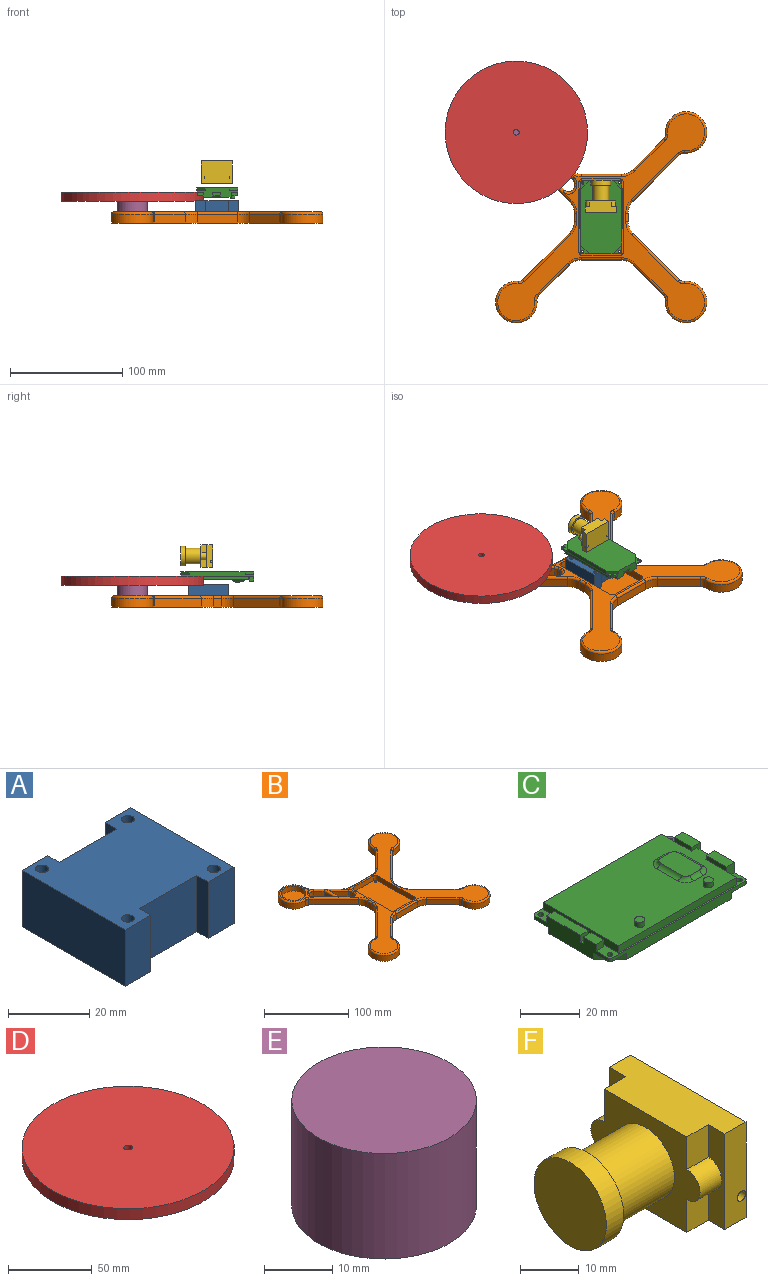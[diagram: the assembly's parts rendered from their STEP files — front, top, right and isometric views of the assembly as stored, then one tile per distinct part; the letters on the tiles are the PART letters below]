
ASSEMBLY  parts=6 mates=3
PART A: 18 faces, bbox 38x36x17 mm
  f0: plane 36x17.02mm, normal (1,0,0), area 612.6mm2, adj f1,f15,f16,f17
  f1: plane 17.02x9mm, normal (0,1,0), area 153.2mm2, adj f0,f2,f16,f17
  f2: plane 17.02x4mm, normal (-1,0,0), area 68.1mm2, adj f1,f3,f16,f17
  f3: plane 20x17.02mm, normal (0,1,0), area 340.4mm2, adj f2,f4,f16,f17
  f4: plane 17.02x4mm, normal (1,0,0), area 68.1mm2, adj f3,f5,f16,f17
  f5: plane 17.02x9mm, normal (0,1,0), area 153.2mm2, adj f4,f6,f16,f17
  f6: plane 36x17.02mm, normal (-1,0,0), area 612.6mm2, adj f5,f7,f16,f17
  f7: plane 17.02x9mm, normal (0,-1,0), area 153.2mm2, adj f6,f8,f16,f17
  f8: plane 17.02x4mm, normal (1,0,0), area 68.1mm2, adj f7,f9,f16,f17
  f9: plane 20x17.02mm, normal (0,-1,0), area 340.4mm2, adj f8,f10,f16,f17
  f10: plane 17.02x4mm, normal (-1,0,0), area 68.1mm2, adj f9,f15,f16,f17
  f11: cylinder r=1.6mm len=17.02mm, axis (0,0,-1), area 171.1mm2, adj f16,f17
  f12: cylinder r=1.6mm len=17.02mm, axis (0,0,-1), area 171.1mm2, adj f16,f17
  f13: cylinder r=1.6mm len=17.02mm, axis (0,0,-1), area 171.1mm2, adj f16,f17
  f14: cylinder r=1.6mm len=17.02mm, axis (0,0,-1), area 171.1mm2, adj f16,f17
  f15: plane 17.02x9mm, normal (0,-1,0), area 153.2mm2, adj f0,f10,f16,f17
  f16: plane 38x36mm, normal (0,0,1), area 1175.8mm2, adj f0,f1,f2,f3,f4,f5,f6,f7
  f17: plane 38x36mm, normal (0,0,-1), area 1175.8mm2, adj f0,f1,f2,f3,f4,f5,f6,f7
PART B: 109 faces, bbox 191.4x191.4x10 mm
  f0: plane 184.37x184.37mm, normal (0,0,1), area 6055.4mm2, adj f27,f28,f29,f30,f55,f56,f57,f60
  f1: plane 8.81x8.81mm, normal (0.71,0.71,0), area 99.6mm2, adj f4,f51,f68,f99
  f2: plane 8.87x8.87mm, normal (-0.71,-0.71,0), area 100.4mm2, adj f4,f53,f55,f93
  f3: plane 38.8x38.8mm, normal (0,0,1), area 230.2mm2, adj f25,f54,f55,f58,f59,f62,f63,f67
  f4: plane 188.37x188.37mm, normal (0,0,-1), area 11909.2mm2, adj f1,f2,f5,f6,f7,f8,f9,f10
  f5: plane 41.52x41.52mm, normal (-0.71,0.71,0), area 469.8mm2, adj f4,f40,f42,f77
  f6: plane 27.32x27.32mm, normal (0.71,-0.71,0), area 309.1mm2, adj f4,f34,f43,f85
  f7: plane 27.32x27.32mm, normal (-0.71,-0.71,0), area 309.1mm2, adj f4,f35,f44,f92
  f8: plane 41.52x41.52mm, normal (-0.71,-0.71,0), area 469.8mm2, adj f4,f41,f49,f68
  f9: cylinder r=18.53mm len=37.05mm, axis (0,0,-1), area 726.3mm2, adj f4,f42,f43,f81
  f10: cylinder r=18.53mm len=37.05mm, axis (0,0,-1), area 726.3mm2, adj f4,f44,f45,f88
  f11: plane 41.52x41.52mm, normal (0.71,0.71,0), area 469.8mm2, adj f4,f36,f45,f84
  f12: plane 41.52x41.52mm, normal (0.71,-0.71,0), area 469.8mm2, adj f4,f37,f46,f76
  f13: cylinder r=18.53mm len=37.05mm, axis (0,0,-1), area 726.3mm2, adj f4,f46,f47,f72
  f14: plane 27.32x27.32mm, normal (-0.71,0.71,0), area 309.1mm2, adj f4,f38,f47,f69
  f15: plane 27.32x27.32mm, normal (0.71,0.71,0), area 309.1mm2, adj f4,f39,f48,f55
  f16: cylinder r=18.53mm len=37.05mm, axis (0,0,-1), area 726.3mm2, adj f4,f48,f49,f62
  f17: plane 8x7.29mm, normal (-1,0,0), area 58.3mm2, adj f4,f40,f41,f73
  f18: plane 35.69x8mm, normal (0,1,0), area 285.5mm2, adj f4,f38,f39,f61
  f19: plane 8x7.29mm, normal (1,0,0), area 58.3mm2, adj f4,f36,f37,f80
  f20: plane 35.69x8mm, normal (0,-1,0), area 285.5mm2, adj f4,f34,f35,f89
  f21: cylinder r=18.53mm len=8mm, axis (0,0,1), area 12.6mm2, adj f4,f50,f53,f59
  f22: plane 15.94x15.94mm, normal (0.71,0.71,0), area 180.4mm2, adj f4,f50,f68,f97
  f23: plane 8x2.83mm, normal (-1,0,0), area 22.6mm2, adj f4,f51,f52,f60
  f24: plane 14.46x14.46mm, normal (-0.71,-0.71,0), area 163.6mm2, adj f4,f52,f55,f95
  f25: cylinder r=14.53mm len=29.05mm, axis (0,0,1), area 638.9mm2, adj f3,f26
  f26: plane 29.05x29.05mm, normal (0,0,1), area 662.8mm2, adj f25
  f27: plane 61.1x7mm, normal (-1,0,0), area 427.7mm2, adj f0,f31,f105,f108
  f28: plane 32.7x7mm, normal (0,-1,0), area 228.9mm2, adj f0,f31,f105,f106
  f29: plane 61.1x7mm, normal (1,0,0), area 427.7mm2, adj f0,f31,f106,f107
  f30: plane 32.7x7mm, normal (0,1,0), area 228.9mm2, adj f0,f31,f107,f108
  f31: plane 68.4x40mm, normal (0,0,1), area 2712mm2, adj f27,f28,f29,f30,f101,f102,f103,f104
  f32: plane 14.14x8mm, normal (1,0,0), area 113.1mm2, adj f4,f64,f95,f99
  f33: plane 14.14x8mm, normal (-1,0,0), area 113.1mm2, adj f4,f64,f93,f97
  f34: cylinder r=15mm len=10.61mm, axis (0,0,1), area 94.2mm2, adj f4,f6,f20,f87
  f35: cylinder r=15mm len=10.61mm, axis (0,0,-1), area 94.2mm2, adj f4,f7,f20,f91
  f36: cylinder r=15mm len=10.61mm, axis (0,0,1), area 94.2mm2, adj f4,f11,f19,f82
  f37: cylinder r=15mm len=10.61mm, axis (0,0,-1), area 94.2mm2, adj f4,f12,f19,f78
  f38: cylinder r=15mm len=10.61mm, axis (0,0,1), area 94.2mm2, adj f4,f14,f18,f66
  f39: cylinder r=15mm len=10.61mm, axis (0,0,-1), area 94.2mm2, adj f4,f15,f18,f57
  f40: cylinder r=15mm len=10.61mm, axis (0,0,-1), area 94.2mm2, adj f4,f5,f17,f75
  f41: cylinder r=15mm len=10.61mm, axis (0,0,1), area 94.2mm2, adj f4,f8,f17,f71
  f42: cylinder r=5mm len=8mm, axis (0,0,-1), area 35.2mm2, adj f4,f5,f9,f79
  f43: cylinder r=5mm len=8mm, axis (0,0,-1), area 35.2mm2, adj f4,f6,f9,f83
  f44: cylinder r=5mm len=8mm, axis (0,0,-1), area 35.2mm2, adj f4,f7,f10,f90
  f45: cylinder r=5mm len=8mm, axis (0,0,-1), area 35.2mm2, adj f4,f10,f11,f86
  f46: cylinder r=5mm len=8mm, axis (0,0,-1), area 35.2mm2, adj f4,f12,f13,f74
  f47: cylinder r=5mm len=8mm, axis (0,0,-1), area 35.2mm2, adj f4,f13,f14,f70
  f48: cylinder r=5mm len=8mm, axis (0,0,-1), area 35.2mm2, adj f4,f15,f16,f58
  f49: cylinder r=5mm len=8mm, axis (0,0,-1), area 35.2mm2, adj f4,f8,f16,f67
  f50: cylinder r=5mm len=8mm, axis (0,0,1), area 64.5mm2, adj f4,f21,f22,f63
  f51: cylinder r=5mm len=8.54mm, axis (0,0,-1), area 94.2mm2, adj f1,f4,f23,f65
  f52: cylinder r=5mm len=8mm, axis (0,0,-1), area 31.4mm2, adj f4,f23,f24,f56
  f53: cylinder r=5mm len=8mm, axis (0,0,1), area 64.5mm2, adj f2,f4,f21,f54
  f54: torus R=7mm, axis (0,0,1), area 29mm2, adj f3,f53,f55,f59
  f55: cylinder r=2mm len=35.97mm, axis (0.71,-0.71,0), area 234.7mm2, adj f0,f2,f3,f15,f24,f54,f56,f57
  f56: torus R=7mm, axis (0,0,1), area 14.1mm2, adj f0,f52,f55,f60
  f57: torus R=17mm, axis (0,0,1), area 38.8mm2, adj f0,f39,f55,f61
  f58: torus R=7mm, axis (0,0,1), area 15.8mm2, adj f3,f48,f55,f62
  f59: torus R=16.53mm, axis (0,0,1), area 4.8mm2, adj f3,f21,f54,f63
  f60: cylinder r=2mm len=2.83mm, axis (0,-1,0), area 8.9mm2, adj f0,f23,f56,f65
  f61: cylinder r=2mm len=35.69mm, axis (1,0,0), area 112.1mm2, adj f0,f18,f57,f66
  f62: torus R=16.53mm, axis (0,0,1), area 274mm2, adj f3,f16,f58,f67
  f63: torus R=7mm, axis (0,0,1), area 29mm2, adj f3,f50,f59,f68
  f64: cylinder r=2mm len=22.63mm, axis (0,1,0), area 108.2mm2, adj f32,f33,f94,f96,f98,f100
  f65: torus R=7mm, axis (0,0,1), area 42.4mm2, adj f0,f51,f60,f68
  f66: torus R=17mm, axis (0,0,1), area 38.8mm2, adj f0,f38,f61,f69
  f67: torus R=7mm, axis (0,0,1), area 15.8mm2, adj f3,f49,f62,f68
  f68: cylinder r=2mm len=44.35mm, axis (-0.71,0.71,0), area 304.1mm2, adj f0,f1,f3,f8,f22,f63,f65,f67
  f69: cylinder r=2mm len=28.74mm, axis (0.71,0.71,0), area 121.4mm2, adj f0,f14,f66,f70
  f70: torus R=7mm, axis (0,0,1), area 15.8mm2, adj f0,f47,f69,f72
  f71: torus R=17mm, axis (0,0,1), area 38.8mm2, adj f0,f41,f68,f73
  f72: torus R=16.53mm, axis (0,0,1), area 274mm2, adj f0,f13,f70,f74
  f73: cylinder r=2mm len=7.29mm, axis (0,1,0), area 22.9mm2, adj f0,f17,f71,f75
  f74: torus R=7mm, axis (0,0,1), area 15.8mm2, adj f0,f46,f72,f76
  f75: torus R=17mm, axis (0,0,1), area 38.8mm2, adj f0,f40,f73,f77
  f76: cylinder r=2mm len=42.94mm, axis (-0.71,-0.71,0), area 184.5mm2, adj f0,f12,f74,f78
  f77: cylinder r=2mm len=42.94mm, axis (0.71,0.71,0), area 184.5mm2, adj f0,f5,f75,f79
  f78: torus R=17mm, axis (0,0,1), area 38.8mm2, adj f0,f37,f76,f80
  f79: torus R=7mm, axis (0,0,1), area 15.8mm2, adj f0,f42,f77,f81
  f80: cylinder r=2mm len=7.29mm, axis (0,-1,0), area 22.9mm2, adj f0,f19,f78,f82
  f81: torus R=16.53mm, axis (0,0,1), area 274mm2, adj f0,f9,f79,f83
  f82: torus R=17mm, axis (0,0,1), area 38.8mm2, adj f0,f36,f80,f84
  f83: torus R=7mm, axis (0,0,1), area 15.8mm2, adj f0,f43,f81,f85
  f84: cylinder r=2mm len=42.94mm, axis (0.71,-0.71,0), area 184.5mm2, adj f0,f11,f82,f86
  f85: cylinder r=2mm len=28.74mm, axis (-0.71,-0.71,0), area 121.4mm2, adj f0,f6,f83,f87
  f86: torus R=7mm, axis (0,0,1), area 15.8mm2, adj f0,f45,f84,f88
  f87: torus R=17mm, axis (0,0,1), area 38.8mm2, adj f0,f34,f85,f89
  f88: torus R=16.53mm, axis (0,0,1), area 274mm2, adj f0,f10,f86,f90
  f89: cylinder r=2mm len=35.69mm, axis (-1,0,0), area 112.1mm2, adj f0,f20,f87,f91
  f90: torus R=7mm, axis (0,0,1), area 15.8mm2, adj f0,f44,f88,f92
  f91: torus R=17mm, axis (0,0,1), area 38.8mm2, adj f0,f35,f89,f92
  f92: cylinder r=2mm len=28.74mm, axis (-0.71,0.71,0), area 121.4mm2, adj f0,f7,f90,f91
  f93: cylinder r=1mm len=8mm, axis (0,0,1), area 6.3mm2, adj f2,f4,f33,f94
  f94: bspline ~2.29x2.26mm, area 1.6mm2, adj f55,f64,f93
  f95: cylinder r=1mm len=8mm, axis (0,0,-1), area 18.8mm2, adj f4,f24,f32,f96
  f96: bspline ~7.24x3.71mm, area 7.9mm2, adj f55,f64,f95
  f97: cylinder r=1mm len=8mm, axis (0,0,1), area 18.8mm2, adj f4,f22,f33,f98
  f98: bspline ~7.24x3.71mm, area 7.9mm2, adj f64,f68,f97
  f99: cylinder r=1mm len=8mm, axis (0,0,-1), area 6.3mm2, adj f1,f4,f32,f100
  f100: bspline ~2.29x2.07mm, area 1.6mm2, adj f64,f68,f99
  f101: cylinder r=1mm len=3mm, axis (0,0,1), area 18.8mm2, adj f4,f31
  f102: cylinder r=1mm len=3mm, axis (0,0,1), area 18.8mm2, adj f4,f31
  f103: cylinder r=1mm len=3mm, axis (0,0,1), area 18.8mm2, adj f4,f31
  f104: cylinder r=1mm len=3mm, axis (0,0,1), area 18.8mm2, adj f4,f31
  f105: cylinder r=3.65mm len=7mm, axis (0,0,1), area 40.1mm2, adj f0,f27,f28,f31
  f106: cylinder r=3.65mm len=7mm, axis (0,0,-1), area 40.1mm2, adj f0,f28,f29,f31
  f107: cylinder r=3.65mm len=7mm, axis (0,0,1), area 40.1mm2, adj f0,f29,f30,f31
  f108: cylinder r=3.65mm len=7mm, axis (0,0,-1), area 40.1mm2, adj f0,f27,f30,f31
PART C: 60 faces, bbox 65x36.5x9 mm
  f0: plane 58.7x35.6mm, normal (0,0,1), area 1787.7mm2, adj f1,f24,f25,f26,f27,f29,f31,f48
  f1: plane 15x3mm, normal (1,0,0), area 45mm2, adj f0,f2,f26,f50
  f2: plane 65x36.5mm, normal (0,0,1), area 195mm2, adj f1,f6,f7,f8,f9,f10,f11,f12
  f3: plane 7.67x7.67mm, normal (0,0,-1), area 26mm2, adj f9,f10,f11,f16,f23
  f4: plane 7.67x7.67mm, normal (0,0,-1), area 26mm2, adj f11,f12,f15,f17,f22
  f5: plane 7.67x7.67mm, normal (0,0,-1), area 26mm2, adj f7,f8,f9,f13,f20
  f6: cylinder r=1mm len=1.4mm, axis (0,0,-1), area 2.2mm2, adj f2,f7,f17,f18
  f7: plane 63x4mm, normal (0,1,0), area 217.3mm2, adj f2,f5,f6,f8,f18,f19,f20,f21
  f8: cylinder r=1mm len=1.4mm, axis (0,0,-1), area 2.2mm2, adj f2,f5,f7,f9
  f9: plane 34.5x6.8mm, normal (-1,0,0), area 164.9mm2, adj f2,f3,f5,f8,f10,f19,f20,f23
  f10: cylinder r=1mm len=1.4mm, axis (0,0,-1), area 2.2mm2, adj f2,f3,f9,f11
  f11: plane 63x4mm, normal (0,-1,0), area 217.3mm2, adj f2,f3,f4,f10,f12,f19,f22,f23
  f12: cylinder r=1mm len=1.4mm, axis (0,0,-1), area 2.2mm2, adj f2,f4,f11,f17
  f13: cylinder r=1mm len=2mm, axis (0,0,-1), area 8.8mm2, adj f2,f5
  f14: cylinder r=1mm len=2mm, axis (0,0,-1), area 8.8mm2, adj f2,f18
  f15: cylinder r=1mm len=2mm, axis (0,0,-1), area 8.8mm2, adj f2,f4
  f16: cylinder r=1mm len=2mm, axis (0,0,-1), area 8.8mm2, adj f2,f3
  f17: plane 34.5x8.3mm, normal (1,0,0), area 179.9mm2, adj f2,f4,f6,f12,f18,f19,f21,f22
  f18: plane 7.67x7.67mm, normal (0,0,-1), area 26mm2, adj f6,f7,f14,f17,f21
  f19: plane 65x36.5mm, normal (0,0,-1), area 2254.9mm2, adj f7,f9,f11,f17,f20,f21,f22,f23
  f20: plane 7.67x7.67mm, normal (-0.71,0.71,0), area 28.2mm2, adj f5,f7,f9,f19
  f21: plane 7.67x7.67mm, normal (0.71,0.71,0), area 28.2mm2, adj f7,f17,f18,f19
  f22: plane 7.67x7.67mm, normal (0.71,-0.71,0), area 28.2mm2, adj f4,f11,f17,f19
  f23: plane 7.67x7.67mm, normal (-0.71,-0.71,0), area 28.2mm2, adj f3,f9,f11,f19
  f24: plane 14x3mm, normal (1,0,0), area 42mm2, adj f0,f2,f25,f49
  f25: plane 56x3mm, normal (0,1,0), area 168mm2, adj f0,f2,f24,f27
  f26: plane 56x3mm, normal (0,-1,0), area 168mm2, adj f0,f1,f2,f27
  f27: plane 35.6x3mm, normal (-1,0,0), area 106.8mm2, adj f0,f2,f25,f26
  f28: plane 3.5x3.5mm, normal (0,0,1), area 9.6mm2, adj f29
  f29: cylinder r=1.75mm len=3.5mm, axis (0,0,-1), area 22mm2, adj f0,f28
  f30: plane 3.5x3.5mm, normal (0,0,1), area 9.6mm2, adj f31
  f31: cylinder r=1.75mm len=3.5mm, axis (0,0,-1), area 22mm2, adj f0,f30
  f32: plane 16x3.7mm, normal (0,0,1), area 59.2mm2, adj f9,f33,f34,f35
  f33: plane 3.7x2.8mm, normal (0,1,0), area 10.4mm2, adj f2,f9,f32,f34
  f34: plane 16x2.8mm, normal (1,0,0), area 44.8mm2, adj f2,f32,f33,f35
  f35: plane 3.7x2.8mm, normal (0,-1,0), area 10.4mm2, adj f2,f9,f32,f34
  f36: plane 6x3.7mm, normal (0,0,1), area 22.2mm2, adj f9,f37,f38,f39
  f37: plane 3.7x2.8mm, normal (0,1,0), area 10.4mm2, adj f2,f9,f36,f38
  f38: plane 6x2.8mm, normal (1,0,0), area 16.8mm2, adj f2,f36,f37,f39
  f39: plane 3.7x2.8mm, normal (0,-1,0), area 10.4mm2, adj f2,f9,f36,f38
  f40: plane 9.5x4mm, normal (0,0,1), area 38mm2, adj f17,f41,f42,f43
  f41: plane 4.3x4mm, normal (0,-1,0), area 17.2mm2, adj f2,f17,f40,f42
  f42: plane 9.5x4.3mm, normal (-1,0,0), area 40.9mm2, adj f2,f40,f41,f43
  f43: plane 4.3x4mm, normal (0,1,0), area 17.2mm2, adj f2,f17,f40,f42
  f44: plane 8.3x4mm, normal (0,0,1), area 33.2mm2, adj f17,f45,f46,f47
  f45: plane 4.3x4mm, normal (0,1,0), area 17.2mm2, adj f2,f17,f44,f47
  f46: plane 4.3x4mm, normal (0,-1,0), area 17.2mm2, adj f2,f17,f44,f47
  f47: plane 8.3x4.3mm, normal (-1,0,0), area 35.7mm2, adj f2,f44,f45,f46
  f48: plane 6.6x3mm, normal (1,0,0), area 19.8mm2, adj f0,f2,f49,f50
  f49: plane 3x2.7mm, normal (0,1,0), area 8.1mm2, adj f0,f2,f24,f48
  f50: plane 3x2.7mm, normal (0,-1,0), area 8.1mm2, adj f0,f1,f2,f48
  f51: plane 14x8.5mm, normal (0,0,1), area 115.6mm2, adj f52,f53,f54,f55,f56,f57,f58,f59
  f52: cylinder r=2mm len=4.5mm, axis (1,0,0), area 10.9mm2, adj f0,f51,f53,f54
  f53: torus R=3.87mm, axis (0,0,1), area 10.7mm2, adj f0,f51,f52,f55
  f54: torus R=3.87mm, axis (0,0,1), area 10.7mm2, adj f0,f51,f52,f56
  f55: cylinder r=2mm len=10mm, axis (0,1,0), area 24.3mm2, adj f0,f51,f53,f57
  f56: cylinder r=2mm len=10mm, axis (0,-1,0), area 24.3mm2, adj f0,f51,f54,f58
  f57: torus R=3.87mm, axis (0,0,1), area 10.7mm2, adj f0,f51,f55,f59
  f58: torus R=3.87mm, axis (0,0,1), area 10.7mm2, adj f0,f51,f56,f59
  f59: cylinder r=2mm len=4.5mm, axis (1,0,0), area 10.9mm2, adj f0,f51,f57,f58
PART D: 4 faces, bbox 127x127x8 mm
  f0: cylinder r=2.5mm len=8mm, axis (0,0,-1), area 125.7mm2, adj f2,f3
  f1: cylinder r=63.5mm len=127mm, axis (0,0,-1), area 3191.9mm2, adj f2,f3
  f2: plane 127x127mm, normal (0,0,1), area 12648.1mm2, adj f0,f1
  f3: plane 127x127mm, normal (0,0,-1), area 12648.1mm2, adj f0,f1
PART E: 3 faces, bbox 27.1x27.1x18.9 mm
  f0: cylinder r=13.53mm len=27.05mm, axis (0,0,-1), area 1608.1mm2, adj f1,f2
  f1: plane 27.05x27.05mm, normal (0,0,1), area 574.7mm2, adj f0
  f2: plane 27.05x27.05mm, normal (0,0,-1), area 574.7mm2, adj f0
PART F: 22 faces, bbox 28.5x28.2x20 mm
  f0: plane 20x4.16mm, normal (-1,0,0), area 63.9mm2, adj f2,f4,f6,f12,f16,f17
  f1: plane 20x4mm, normal (-1,0,0), area 63.9mm2, adj f2,f5,f6,f13,f14,f15
  f2: plane 28x10.3mm, normal (0,0,1), area 246.8mm2, adj f0,f1,f3,f4,f5,f11,f15,f16
  f3: plane 28x20mm, normal (1,0,0), area 560mm2, adj f2,f4,f5,f6
  f4: plane 20x5.1mm, normal (0,1,0), area 98.9mm2, adj f0,f2,f3,f6,f10
  f5: plane 20x5.1mm, normal (0,-1,0), area 98.9mm2, adj f1,f2,f3,f6,f8
  f6: plane 28x10.3mm, normal (0,0,-1), area 246.8mm2, adj f0,f1,f3,f4,f5,f11,f12,f13
  f7: plane 2x2mm, normal (0,-1,0), area 3.1mm2, adj f8
  f8: cylinder r=1mm len=3mm, axis (0,-1,0), area 18.8mm2, adj f5,f7
  f9: plane 2x2mm, normal (0,1,0), area 3.1mm2, adj f10
  f10: cylinder r=1mm len=3mm, axis (0,1,0), area 18.8mm2, adj f4,f9
  f11: plane 27.36x20mm, normal (-1,0,0), area 278.2mm2, adj f2,f6,f12,f13,f14,f15,f16,f17
  f12: plane 6.8x5.2mm, normal (0,1,0), area 35.4mm2, adj f0,f6,f11,f17
  f13: plane 6.8x5.2mm, normal (0,-1,0), area 35.4mm2, adj f1,f6,f11,f14
  f14: cylinder r=3.2mm len=6.4mm, axis (1,0,0), area 52.3mm2, adj f1,f11,f13,f15
  f15: plane 6.8x5.2mm, normal (0,-1,0), area 35.4mm2, adj f1,f2,f11,f14
  f16: plane 6.8x5.2mm, normal (0,1,0), area 35.4mm2, adj f0,f2,f11,f17
  f17: extruded ~6.4x5.2mm, area 52.3mm2, adj f0,f11,f12,f16
  f18: cylinder r=7mm len=14mm, axis (1,0,0), area 615.8mm2, adj f11,f21
  f19: plane 17.5x17.5mm, normal (-1,0,0), area 240.5mm2, adj f20
  f20: cylinder r=8.75mm len=17.5mm, axis (1,0,0), area 230.9mm2, adj f19,f21
  f21: plane 17.5x17.5mm, normal (1,0,0), area 86.6mm2, adj f18,f20
PLACE A t=(0.4,7.41,-2)mm
PLACE B t=(0.4,-0.39,-5)mm
PLACE C rot(axis=(0.71,-0.71,0),180deg) t=(0.4,-0.39,21.85)mm
PLACE D t=(-75.26,75.27,14.46)mm
PLACE E t=(-75.26,75.27,-4.46)mm
PLACE F rot(axis=(0,0,-1),90deg) t=(0,17.6,40.4)mm
MATE planar A.f17 <-> B.f31  axis (0,0,-1) through (0.4,7.41,-2)mm
MATE cylindrical E.f0 <-> B.f16  axis (0,0,-1) through (-75.26,75.27,5)mm
MATE cylindrical D.f1 <-> E.f0  axis (0,0,-1) through (-75.26,75.27,14.46)mm
